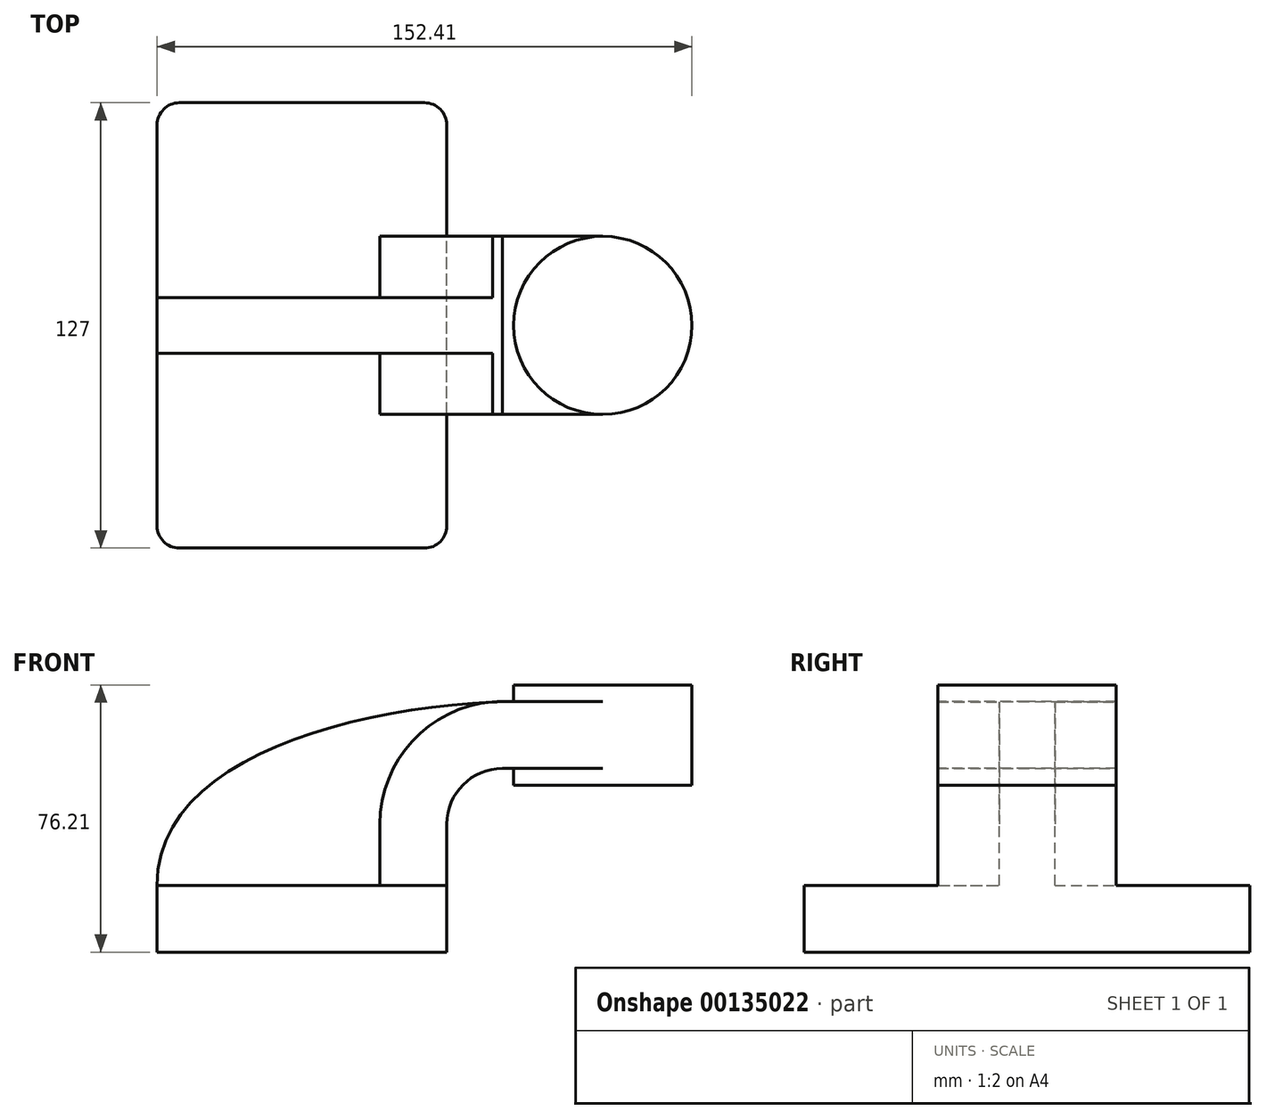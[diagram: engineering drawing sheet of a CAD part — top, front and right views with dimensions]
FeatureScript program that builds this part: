
annotation { "Feature Type Name" : "Feature", "Feature Type Description" : "" }
export const myFeature = defineFeature(function(context is Context, id is Id, definition is map)
    precondition{}
    {
        {
            var Q0;
            Q0=qCreatedBy(makeId("Front.planeOp"),FACE);
            var sketch = newSketch(context, id + "F0", { "sketchPlane" : qUnion([Q0])});
            skLineSegment(sketch, "E0.bottom", {"start": v(-41.28, -9.53) * mm, "end": v(41.28, -9.53) * mm});
            skLineSegment(sketch, "E0.top", {"start": v(-41.28, 9.53) * mm, "end": v(41.28, 9.53) * mm});
            skLineSegment(sketch, "E0.left", {"start": v(-41.28, -9.53) * mm, "end": v(-41.28, 9.53) * mm});
            skLineSegment(sketch, "E0.right", {"start": v(41.28, -9.53) * mm, "end": v(41.28, 9.53) * mm});
            skPoint(sketch, "E0.middle", {"position": v(0, 0) * mm});
            skLineSegment(sketch, "E1.bottom", {"start": v(60.32, 38.1) * mm, "end": v(111.12, 38.1) * mm});
            skLineSegment(sketch, "E1.top", {"start": v(60.32, 66.67) * mm, "end": v(111.12, 66.67) * mm});
            skLineSegment(sketch, "E1.left", {"start": v(60.32, 38.1) * mm, "end": v(60.32, 66.67) * mm});
            skLineSegment(sketch, "E1.right", {"start": v(111.12, 38.1) * mm, "end": v(111.12, 66.67) * mm});
            skPoint(sketch, "E1.middle", {"position": v(85.72, 52.39) * mm});
            skLineSegment(sketch, "E2", {"start": v(41.28, 9.53) * mm, "end": v(41.28, 26.99) * mm});
            skArc(sketch, "E3", {"start": v(41.27, 26.99) * mm, "mid": v(45.92, 38.21) * mm, "end": v(57.15, 42.86) * mm});
            skLineSegment(sketch, "E4", {"start": v(57.15, 42.86) * mm, "end": v(85.72, 42.86) * mm});
            skLineSegment(sketch, "E5.0", {"start": v(57.15, 61.91) * mm, "end": v(85.72, 61.91) * mm});
            skArc(sketch, "E5.1", {"start": v(22.23, 26.99) * mm, "mid": v(32.45, 51.68) * mm, "end": v(57.15, 61.91) * mm});
            skLineSegment(sketch, "E5.2", {"start": v(22.22, 9.53) * mm, "end": v(22.22, 26.99) * mm});
            skLineSegment(sketch, "E6", {"start": v(85.72, 38.1) * mm, "end": v(85.72, 66.67) * mm});
            skFitSpline(sketch, "E7", {"points": [v(-41.28, 9.52) * mm, v(57.15, 61.91) * mm], "startDerivative": vector(-0.44, 107.73) * mm, "endDerivative": vector(131.02, 4.58) * mm});
            skSolve(sketch);
        }
        {
            var Q0;
            Q0=makeQuery(id+"F0.imprint","IMPRINT",FACE,{"disambiguationData":[TD([[makeQuery(id+"F0.imprint","IMPRINT",EDGE,{"derivedFrom":sQuery(id+"F0.wireOp",EDGE,"E0.bottom")}),1.0]])]});
            extrude(context, id + "F1", {"entities" : qUnion([Q0]), "endBound" : BoundingType.SYMMETRIC, "depth" : 127 * mm});
        }
        {
            var Q0;
            {var subQ1=sQuery(id+"F0.wireOp",EDGE,"E2");Q0=makeQuery(id+"F0.imprint","IMPRINT",FACE,{"disambiguationData":[TD([[makeQuery(id+"F0.imprint","IMPRINT",EDGE,{"derivedFrom":subQ1}),1.0]])]});}
            var Q1;
            {var subQ0=sQuery(id+"F0.wireOp",EDGE,"E4");var subQ1=sQuery(id+"F0.wireOp",EDGE,"E1.left");var subQ2=makeQuery(id+"F0.imprint","INTERSECT",VERTEX,{"derivedFrom":[subQ1,subQ0]});Q1=makeQuery(id+"F0.imprint","IMPRINT",FACE,{"disambiguationData":[TD([[makeQuery(id+"F0.imprint","IMPRINT",EDGE,{"disambiguationData":[TD([[subQ2,-1.0]])],"derivedFrom":subQ1}),-1.0]])]});}
            extrude(context, id + "F2", {"entities" : qUnion([Q0, Q1]), "operationType" : NewBodyOperationType.ADD, "endBound" : BoundingType.SYMMETRIC, "depth" : 50.8 * mm});
        }
        {
            var Q0;
            {var subQ3=sQuery(id+"F0.wireOp",EDGE,"E5.2");Q0=makeQuery(id+"F0.imprint","IMPRINT",FACE,{"disambiguationData":[TD([[makeQuery(id+"F0.imprint","IMPRINT",EDGE,{"derivedFrom":subQ3}),1.0]])]});}
            extrude(context, id + "F3", {"entities" : qUnion([Q0]), "operationType" : NewBodyOperationType.ADD, "endBound" : BoundingType.SYMMETRIC, "depth" : 15.88 * mm});
        }
        {
            var Q0;
            {var subQ0=sQuery(id+"F0.wireOp",EDGE,"E1.right");Q0=makeQuery(id+"F0.imprint","IMPRINT",FACE,{"disambiguationData":[TD([[makeQuery(id+"F0.imprint","IMPRINT",EDGE,{"derivedFrom":subQ0}),1.0]])]});}
            var Q1;
            Q1=sQuery(id+"F0.wireOp",EDGE,"E6");
            revolve(context, id + "F4", {"operationType" : NewBodyOperationType.ADD, "entities" : qUnion([Q0]), "axis" : qUnion([Q1]), "revolveType" : RevolveType.FULL});
        }
        {
            var Q0;
            Q0=makeQuery(id+"F1.opExtrude","CAP_EDGE",EDGE,{"disambiguationData":[OSD([sQuery(id+"F0.wireOp",EDGE,"E0.right")])],"isStart":false});
            var Q1;
            Q1=makeQuery(id+"F1.opExtrude","CAP_EDGE",EDGE,{"disambiguationData":[OSD([sQuery(id+"F0.wireOp",EDGE,"E0.left")])],"isStart":false});
            var Q2;
            Q2=makeQuery(id+"F1.opExtrude","CAP_EDGE",EDGE,{"disambiguationData":[OSD([sQuery(id+"F0.wireOp",EDGE,"E0.right")])],"isStart":true});
            var Q3;
            Q3=makeQuery(id+"F1.opExtrude","CAP_EDGE",EDGE,{"disambiguationData":[OSD([sQuery(id+"F0.wireOp",EDGE,"E0.left")])],"isStart":true});
            fillet(context, id + "F5", {"entities" : qUnion([Q0, Q1, Q2, Q3]), "radius" : 6.35 * mm, "tangentPropagation" : true, "allowEdgeOverflow" : false});
        }
    });
